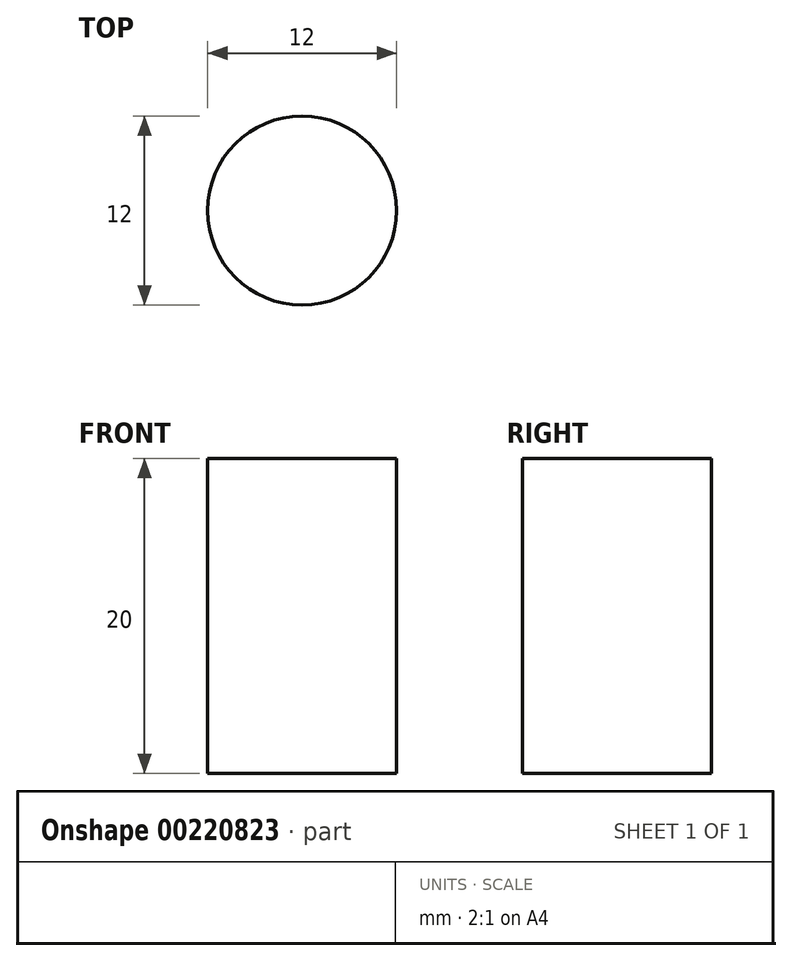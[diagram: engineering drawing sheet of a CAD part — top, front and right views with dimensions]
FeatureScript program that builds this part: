
annotation { "Feature Type Name" : "Feature", "Feature Type Description" : "" }
export const myFeature = defineFeature(function(context is Context, id is Id, definition is map)
    precondition{}
    {
        {
            var Q0;
            Q0=qCreatedBy(makeId("Top.planeOp"),FACE);
            var sketch = newSketch(context, id + "F0", { "sketchPlane" : qUnion([Q0])});
            skCircle(sketch, "E0", {"center": v(0, 0) * mm, "radius": 6 * mm});
            skSolve(sketch);
        }
        {
            var Q0;
            Q0=makeQuery(id+"F0.imprint","IMPRINT",FACE,{"disambiguationData":[TD([[makeQuery(id+"F0.imprint","IMPRINT",EDGE,{"derivedFrom":sQuery(id+"F0.wireOp",EDGE,"E0")}),1.0]])]});
            extrude(context, id + "F1", {"entities" : qUnion([Q0]), "depth" : 20 * mm});
        }
    });
